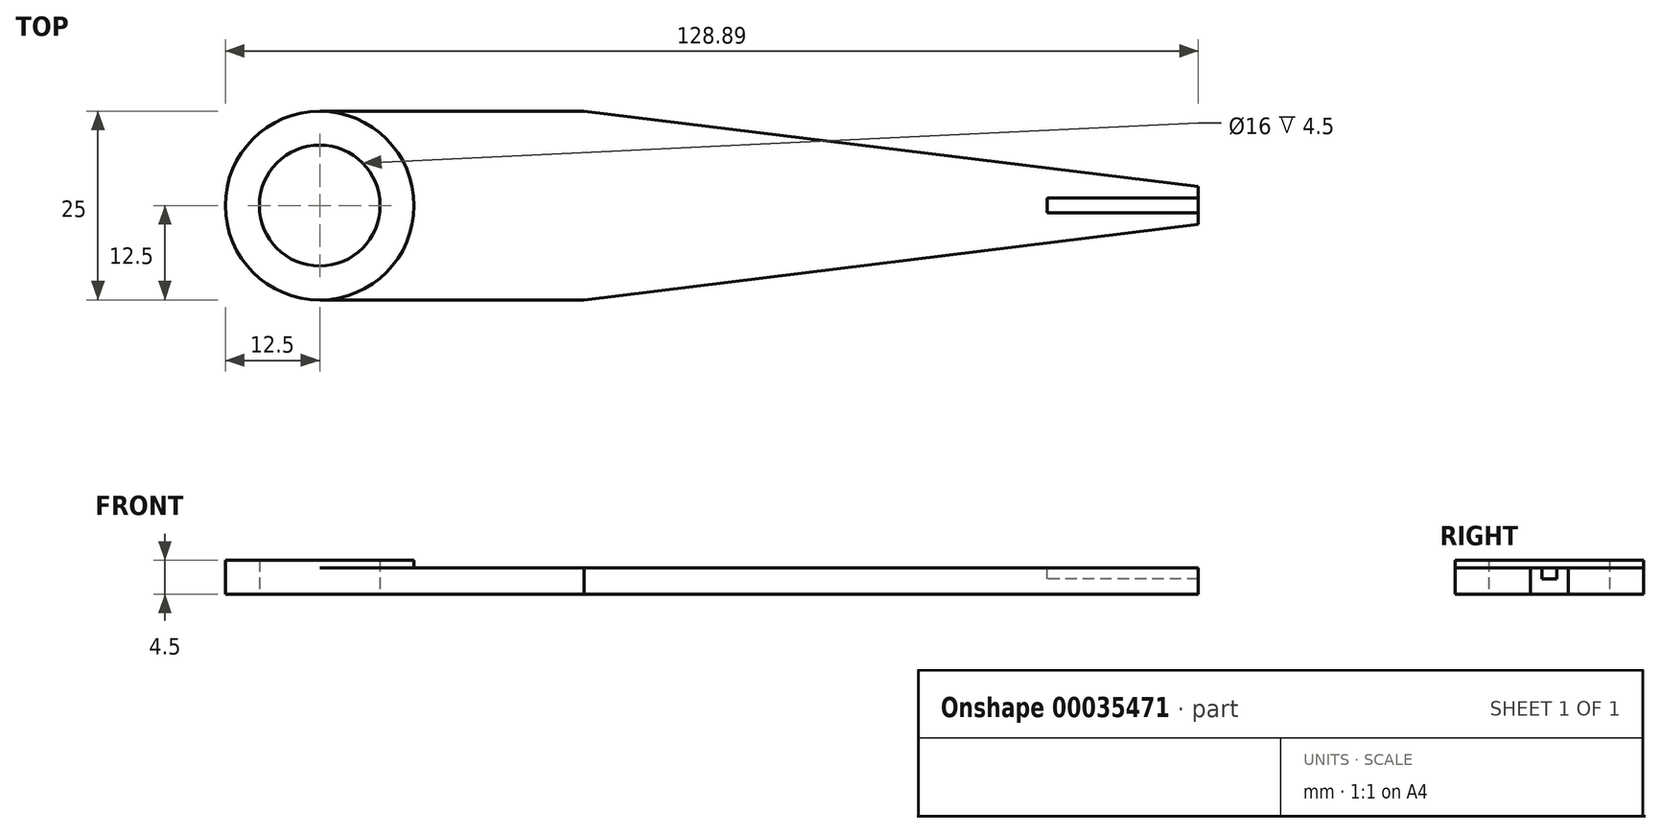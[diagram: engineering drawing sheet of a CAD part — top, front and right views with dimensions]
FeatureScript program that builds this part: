
annotation { "Feature Type Name" : "Feature", "Feature Type Description" : "" }
export const myFeature = defineFeature(function(context is Context, id is Id, definition is map)
    precondition{}
    {
        {
            var Q0;
            Q0=qCreatedBy(makeId("Top.planeOp"),FACE);
            var sketch = newSketch(context, id + "F0", { "sketchPlane" : qUnion([Q0])});
            skCircle(sketch, "E0", {"center": v(0, 0) * mm, "radius": 8 * mm});
            skCircle(sketch, "E1", {"center": v(0, 0) * mm, "radius": 12.5 * mm});
            skLineSegment(sketch, "E2", {"start": v(0, -12.5) * mm, "end": v(35, -12.5) * mm});
            skLineSegment(sketch, "E3", {"start": v(0, 12.5) * mm, "end": v(35, 12.5) * mm});
            skLineSegment(sketch, "E4", {"start": v(35, 12.5) * mm, "end": v(117.7, 12.5) * mm, "construction": true});
            skLineSegment(sketch, "E5", {"start": v(35, 12.5) * mm, "end": v(116.39, 2.5) * mm});
            skLineSegment(sketch, "E6", {"start": v(35, -12.5) * mm, "end": v(118.9, -12.5) * mm, "construction": true});
            skLineSegment(sketch, "E7", {"start": v(35, -12.5) * mm, "end": v(116.39, -2.5) * mm});
            skLineSegment(sketch, "E8", {"start": v(116.39, -2.5) * mm, "end": v(116.39, 2.5) * mm});
            skSolve(sketch);
        }
        {
            var Q0;
            Q0=makeQuery(id+"F0.imprint","IMPRINT",FACE,{"disambiguationData":[TD([[makeQuery(id+"F0.imprint","IMPRINT",EDGE,{"derivedFrom":sQuery(id+"F0.wireOp",EDGE,"E0")}),-1.0]])]});
            var Q1;
            {var subQ1=sQuery(id+"F0.wireOp",EDGE,"E2");Q1=makeQuery(id+"F0.imprint","IMPRINT",FACE,{"disambiguationData":[TD([[makeQuery(id+"F0.imprint","IMPRINT",EDGE,{"derivedFrom":subQ1}),1.0]])]});}
            extrude(context, id + "F1", {"entities" : qUnion([Q0, Q1]), "depth" : 3.5 * mm});
        }
        {
            var Q0;
            Q0=makeQuery(id+"F0.imprint","IMPRINT",FACE,{"disambiguationData":[TD([[makeQuery(id+"F0.imprint","IMPRINT",EDGE,{"derivedFrom":sQuery(id+"F0.wireOp",EDGE,"E0")}),-1.0]])]});
            extrude(context, id + "F2", {"entities" : qUnion([Q0]), "operationType" : NewBodyOperationType.ADD, "depth" : 4.5 * mm});
        }
        {
            var Q0;
            Q0=makeQuery(id+"F1.opExtrude","CAP_FACE",FACE,{"disambiguationData":[OSD([sQuery(id+"F0.wireOp",EDGE,"E0"),sQuery(id+"F0.wireOp",EDGE,"E1"),sQuery(id+"F0.wireOp",EDGE,"E2"),sQuery(id+"F0.wireOp",EDGE,"E3"),sQuery(id+"F0.wireOp",EDGE,"E5"),sQuery(id+"F0.wireOp",EDGE,"E7"),sQuery(id+"F0.wireOp",EDGE,"E8")])],"isStart":false});
            var sketch = newSketch(context, id + "F3", { "sketchPlane" : qUnion([Q0])});
            skLineSegment(sketch, "E9.top", {"start": v(116.39, 1) * mm, "end": v(96.39, 1) * mm});
            skLineSegment(sketch, "E9.left", {"start": v(116.39, 0) * mm, "end": v(116.39, 1) * mm});
            skLineSegment(sketch, "E9.right", {"start": v(96.39, 0) * mm, "end": v(96.39, 1) * mm});
            skLineSegment(sketch, "E10.MirrorCS", {"start": v(116.39, -1) * mm, "end": v(96.39, -1) * mm});
            skLineSegment(sketch, "E11", {"start": v(96.39, -1) * mm, "end": v(96.39, 0) * mm});
            skLineSegment(sketch, "E12", {"start": v(116.39, -1) * mm, "end": v(116.39, 1) * mm});
            skSolve(sketch);
        }
        {
            var Q0;
            {var subQ3=sQuery(id+"F3.wireOp",EDGE,"E9.top");Q0=makeQuery(id+"F3.imprint","IMPRINT",FACE,{"disambiguationData":[TD([[makeQuery(id+"F3.imprint","IMPRINT",EDGE,{"derivedFrom":subQ3}),1.0]])]});}
            extrude(context, id + "F4", {"entities" : qUnion([Q0]), "operationType" : NewBodyOperationType.REMOVE, "oppositeDirection" : true, "depth" : 1.5 * mm});
        }
    });
